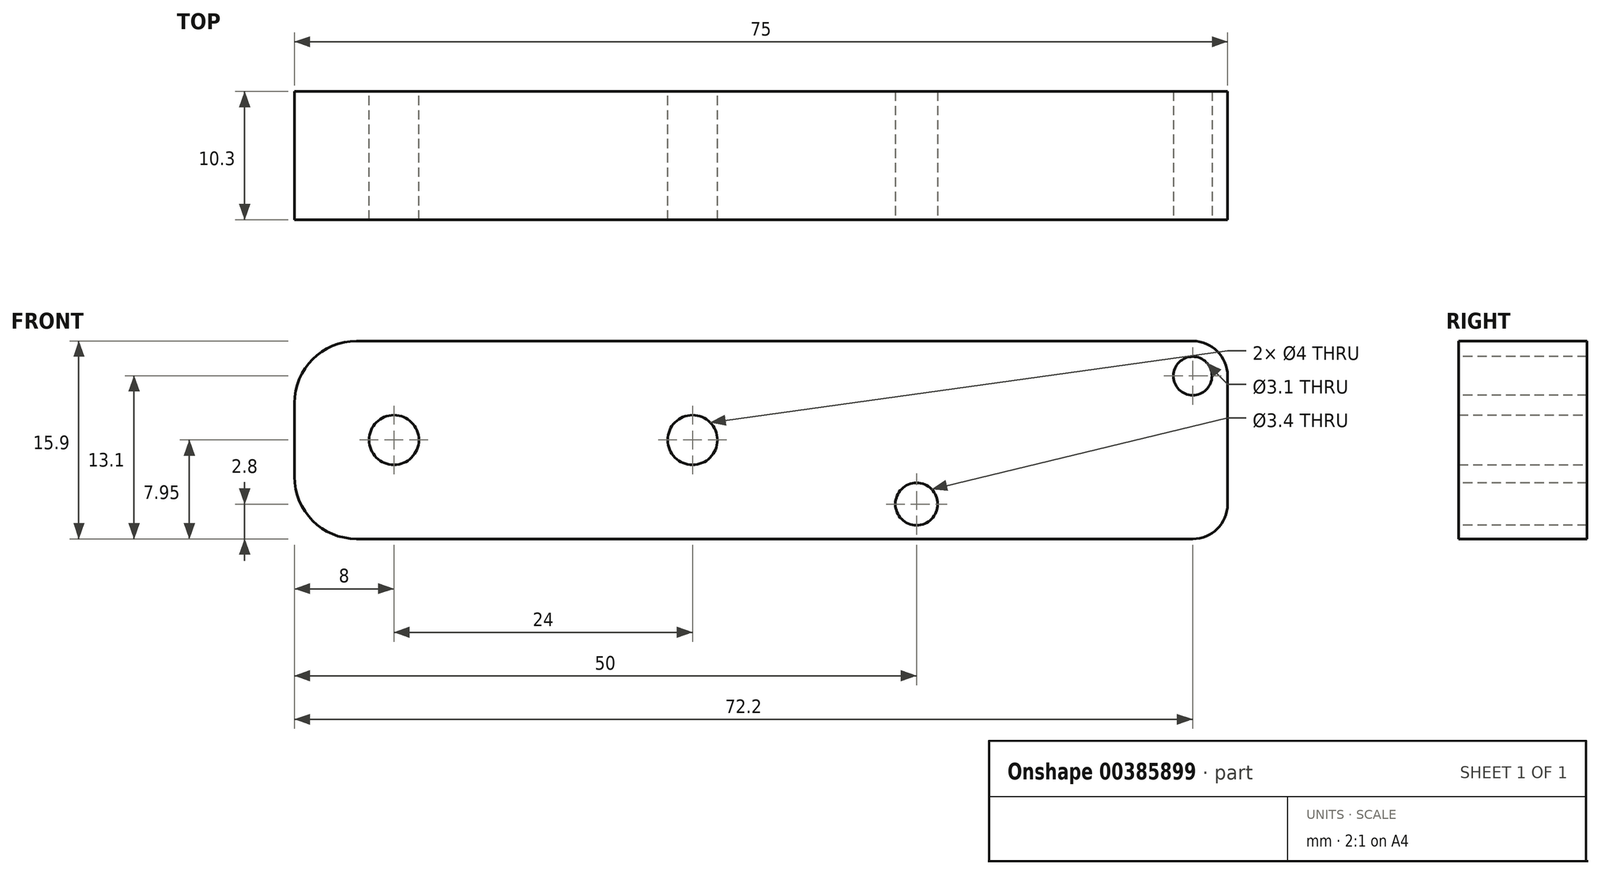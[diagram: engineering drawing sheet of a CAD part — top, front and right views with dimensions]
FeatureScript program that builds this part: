
annotation { "Feature Type Name" : "Feature", "Feature Type Description" : "" }
export const myFeature = defineFeature(function(context is Context, id is Id, definition is map)
    precondition{}
    {
        {
            var Q0;
            Q0=qCreatedBy(makeId("Front.planeOp"),FACE);
            var sketch = newSketch(context, id + "F0", { "sketchPlane" : qUnion([Q0])});
            skLineSegment(sketch, "E0.bottom", {"start": v(0, 0) * mm, "end": v(27.8, 0) * mm});
            skLineSegment(sketch, "E0.top", {"start": v(0, 15.9) * mm, "end": v(27.8, 15.9) * mm});
            skLineSegment(sketch, "E0.left", {"start": v(0, 0) * mm, "end": v(0, 15.9) * mm});
            skLineSegment(sketch, "E0.right", {"start": v(27.8, 0) * mm, "end": v(27.8, 15.9) * mm});
            skSolve(sketch);
        }
        {
            var Q0;
            Q0 = qSketchRegion(id + "F0", true);
            extrude(context, id + "F1", {"entities" : qUnion([Q0]), "depth" : 10.3 * mm});
        }
        {
            var Q0;
            Q0=makeQuery(id+"F1.opExtrude","CAP_FACE",FACE,{"disambiguationData":[OSD([sQuery(id+"F0.wireOp",EDGE,"E0.bottom"),sQuery(id+"F0.wireOp",EDGE,"E0.top"),sQuery(id+"F0.wireOp",EDGE,"E0.left"),sQuery(id+"F0.wireOp",EDGE,"E0.right")])],"isStart":false});
            var sketch = newSketch(context, id + "F2", { "sketchPlane" : qUnion([Q0])});
            skCircle(sketch, "E1", {"center": v(2.8, 2.8) * mm, "radius": 1.7 * mm});
            skCircle(sketch, "E2", {"center": v(25, 13.1) * mm, "radius": 1.55 * mm});
            skSolve(sketch);
        }
        {
            var Q0;
            Q0 = qSketchRegion(id + "F2", true);
            extrude(context, id + "F3", {"entities" : qUnion([Q0]), "operationType" : NewBodyOperationType.REMOVE, "endBound" : BoundingType.THROUGH_ALL, "oppositeDirection" : true, "depth" : 25 * mm});
        }
        {
            var Q0;
            Q0=makeQuery(id+"F1.opExtrude","SWEPT_EDGE",EDGE,{"disambiguationData":[OSD([sQuery(id+"F0.wireOp",EDGE,"E0.bottom"),sQuery(id+"F0.wireOp",EDGE,"E0.left")])]});
            var Q1;
            Q1=makeQuery(id+"F1.opExtrude","SWEPT_EDGE",EDGE,{"disambiguationData":[OSD([sQuery(id+"F0.wireOp",EDGE,"E0.top"),sQuery(id+"F0.wireOp",EDGE,"E0.left")])]});
            var Q2;
            Q2=makeQuery(id+"F1.opExtrude","SWEPT_EDGE",EDGE,{"disambiguationData":[OSD([sQuery(id+"F0.wireOp",EDGE,"E0.bottom"),sQuery(id+"F0.wireOp",EDGE,"E0.right")])]});
            var Q3;
            Q3=makeQuery(id+"F1.opExtrude","SWEPT_EDGE",EDGE,{"disambiguationData":[OSD([sQuery(id+"F0.wireOp",EDGE,"E0.top"),sQuery(id+"F0.wireOp",EDGE,"E0.right")])]});
            fillet(context, id + "F4", {"entities" : qUnion([Q0, Q1, Q2, Q3]), "radius" : 2.8 * mm, "tangentPropagation" : true, "allowEdgeOverflow" : false});
        }
        {
            var Q0;
            Q0=makeQuery(id+"F1.opExtrude","CAP_FACE",FACE,{"disambiguationData":[OSD([sQuery(id+"F0.wireOp",EDGE,"E0.bottom"),sQuery(id+"F0.wireOp",EDGE,"E0.top"),sQuery(id+"F0.wireOp",EDGE,"E0.left"),sQuery(id+"F0.wireOp",EDGE,"E0.right")])],"isStart":false});
            var sketch = newSketch(context, id + "F5", { "sketchPlane" : qUnion([Q0])});
            skLineSegment(sketch, "E3", {"start": v(2.8, 15.9) * mm, "end": v(-42.2, 15.9) * mm});
            skLineSegment(sketch, "E4", {"start": v(-47.2, 10.9) * mm, "end": v(-47.2, 5) * mm});
            skLineSegment(sketch, "E5", {"start": v(-42.2, 0) * mm, "end": v(2.8, 0) * mm});
            skPoint(sketch, "E6.visualSharp", {"position": v(-47.2, 15.9) * mm});
            skArc(sketch, "E6.filletArc", {"start": v(-42.2, 15.9) * mm, "mid": v(-45.74, 14.44) * mm, "end": v(-47.2, 10.9) * mm});
            skPoint(sketch, "E7.visualSharp", {"position": v(-47.2, 0) * mm});
            skArc(sketch, "E7.filletArc", {"start": v(-47.2, 5) * mm, "mid": v(-45.74, 1.46) * mm, "end": v(-42.2, 0) * mm});
            skArc(sketch, "E8.0", {"start": v(0, 2.8) * mm, "mid": v(0.82, 0.82) * mm, "end": v(2.8, 0) * mm});
            skLineSegment(sketch, "E8.1", {"start": v(0, 2.8) * mm, "end": v(0, 13.1) * mm});
            skArc(sketch, "E8.2", {"start": v(2.8, 15.9) * mm, "mid": v(0.82, 15.08) * mm, "end": v(0, 13.1) * mm});
            skSolve(sketch);
        }
        {
            var Q0;
            Q0 = qSketchRegion(id + "F5", true);
            var Q1;
            Q1=makeQuery(id+"F1.opExtrude","CAP_FACE",FACE,{"disambiguationData":[OSD([sQuery(id+"F0.wireOp",EDGE,"E0.bottom"),sQuery(id+"F0.wireOp",EDGE,"E0.top"),sQuery(id+"F0.wireOp",EDGE,"E0.left"),sQuery(id+"F0.wireOp",EDGE,"E0.right")])],"isStart":true});
            extrude(context, id + "F6", {"entities" : qUnion([Q0]), "operationType" : NewBodyOperationType.ADD, "endBound" : BoundingType.UP_TO_SURFACE, "oppositeDirection" : true, "depth" : 10.8 * mm, "endBoundEntityFace" : qUnion([Q1]), "offsetDistance" : 25 * mm});
        }
        {
            var Q0;
            Q0=makeQuery(id+"F6.boolean.opBoolean","MERGE",FACE,{"derivedFrom":[makeQuery(id+"F1.opExtrude","CAP_FACE",FACE,{"disambiguationData":[OSD([sQuery(id+"F0.wireOp",EDGE,"E0.bottom"),sQuery(id+"F0.wireOp",EDGE,"E0.top"),sQuery(id+"F0.wireOp",EDGE,"E0.left"),sQuery(id+"F0.wireOp",EDGE,"E0.right")])],"isStart":true}),makeQuery(id+"F6.opExtrude","CAP_FACE",FACE,{"disambiguationData":[OSD([sQuery(id+"F5.wireOp",EDGE,"E3"),sQuery(id+"F5.wireOp",EDGE,"E4"),sQuery(id+"F5.wireOp",EDGE,"E5"),sQuery(id+"F5.wireOp",EDGE,"E6.filletArc"),sQuery(id+"F5.wireOp",EDGE,"E7.filletArc"),sQuery(id+"F5.wireOp",EDGE,"E8.0"),sQuery(id+"F5.wireOp",EDGE,"E8.1"),sQuery(id+"F5.wireOp",EDGE,"E8.2")])],"isStart":false})]});
            var sketch = newSketch(context, id + "F7", { "sketchPlane" : qUnion([Q0])});
            skLineSegment(sketch, "E9", {"start": v(-27.8, 7.95) * mm, "end": v(47.2, 7.95) * mm, "construction": true});
            skCircle(sketch, "E10", {"center": v(39.2, 7.95) * mm, "radius": 2 * mm});
            skCircle(sketch, "E11", {"center": v(15.2, 7.95) * mm, "radius": 2 * mm});
            skSolve(sketch);
        }
        {
            var Q0;
            Q0 = qSketchRegion(id + "F7", true);
            extrude(context, id + "F8", {"entities" : qUnion([Q0]), "operationType" : NewBodyOperationType.REMOVE, "endBound" : BoundingType.UP_TO_NEXT, "oppositeDirection" : true, "depth" : 19.4 * mm, "offsetDistance" : 25 * mm});
        }
    });
